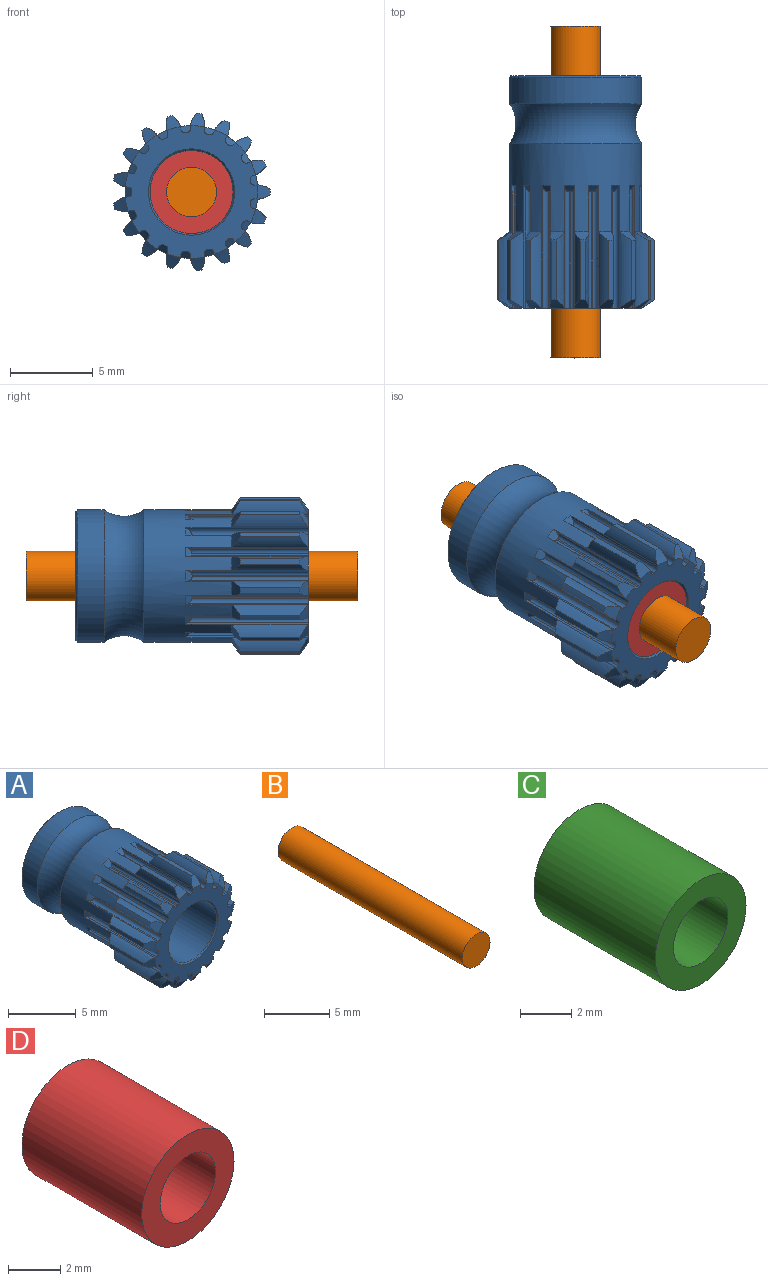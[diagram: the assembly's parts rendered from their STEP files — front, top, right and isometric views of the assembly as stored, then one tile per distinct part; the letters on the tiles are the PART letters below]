
ASSEMBLY  parts=4 mates=3
PART A: 196 faces, bbox 9.5x14x9.5 mm
  f0: cone r=4.38mm half-angle=56.3deg, axis (0,-1,0), area 0.6mm2, adj f21,f42,f43,f88
  f1: cone r=4.38mm half-angle=56.3deg, axis (0,-1,0), area 0.6mm2, adj f24,f50,f51,f88
  f2: cone r=4.38mm half-angle=56.3deg, axis (0,-1,0), area 0.6mm2, adj f25,f53,f54,f88
  f3: cone r=4.38mm half-angle=56.3deg, axis (0,-1,0), area 0.6mm2, adj f26,f59,f60,f88
  f4: cone r=4.38mm half-angle=56.3deg, axis (0,-1,0), area 0.6mm2, adj f12,f62,f63,f88
  f5: cone r=4.38mm half-angle=56.3deg, axis (0,-1,0), area 0.6mm2, adj f13,f65,f66,f88
  f6: cone r=4.38mm half-angle=56.3deg, axis (0,-1,0), area 0.6mm2, adj f14,f68,f69,f88
  f7: cone r=4.38mm half-angle=56.3deg, axis (0,-1,0), area 0.6mm2, adj f15,f82,f83,f88
  f8: cone r=4.38mm half-angle=56.3deg, axis (0,-1,0), area 0.6mm2, adj f16,f17,f80,f88
  f9: cone r=4.38mm half-angle=56.3deg, axis (0,-1,0), area 0.6mm2, adj f18,f77,f78,f88
  f10: cone r=4.38mm half-angle=56.3deg, axis (0,-1,0), area 0.6mm2, adj f19,f74,f75,f88
  f11: cone r=4.38mm half-angle=56.3deg, axis (0,-1,0), area 0.6mm2, adj f20,f39,f40,f88
  f12: extruded ~7x0.63mm, area 3.4mm2, adj f4,f30,f61,f63,f88,f111
  f13: extruded ~7x0.78mm, area 3.4mm2, adj f5,f30,f64,f66,f88,f116
  f14: extruded ~7x0.82mm, area 3.4mm2, adj f6,f30,f67,f69,f88,f121
  f15: extruded ~7x0.75mm, area 3.4mm2, adj f7,f30,f81,f83,f88,f126
  f16: extruded ~7x0.81mm, area 3.4mm2, adj f8,f30,f79,f80,f88,f130
  f17: extruded ~7x0.58mm, area 3.4mm2, adj f8,f30,f79,f80,f88,f131
  f18: extruded ~7x0.75mm, area 3.4mm2, adj f9,f30,f76,f78,f88,f136
  f19: extruded ~7x0.82mm, area 3.4mm2, adj f10,f30,f73,f75,f88,f141
  f20: extruded ~7x0.72mm, area 3.4mm2, adj f11,f30,f38,f40,f88,f157
  f21: extruded ~7x0.81mm, area 3.4mm2, adj f0,f30,f41,f43,f88,f162
  f22: extruded ~7x0.63mm, area 3.4mm2, adj f23,f30,f44,f45,f88,f166
  f23: cone r=4.38mm half-angle=56.3deg, axis (0,-1,0), area 0.6mm2, adj f22,f45,f88,f167
  f24: extruded ~7x0.68mm, area 3.4mm2, adj f1,f30,f49,f51,f88,f179
  f25: extruded ~7x0.8mm, area 3.4mm2, adj f2,f30,f52,f54,f88,f184
  f26: extruded ~7x0.71mm, area 3.4mm2, adj f3,f30,f58,f60,f88,f194
  f27: extruded ~7x0.78mm, area 3.4mm2, adj f30,f70,f72,f88,f146,f195
  f28: cone r=2.55mm half-angle=45deg, axis (0,-1,0), area 2.3mm2, adj f29,f30
  f29: cylinder r=2.5mm len=13.8mm, axis (0,1,0), area 216.8mm2, adj f28,f31
  f30: plane 8x7.99mm, normal (0,-1,0), area 25.4mm2, adj f12,f13,f14,f15,f16,f17,f18,f19
  f31: cone r=2.55mm half-angle=45deg, axis (0,1,0), area 2.3mm2, adj f29,f32
  f32: plane 7.8x7.8mm, normal (0,1,0), area 26.5mm2, adj f31,f33
  f33: cone r=3.95mm half-angle=45deg, axis (0,-1,0), area 3.5mm2, adj f32,f34
  f34: cylinder r=4mm len=8mm, axis (0,1,0), area 40.2mm2, adj f33,f87
  f35: cone r=4.38mm half-angle=56.3deg, axis (0,1,0), area 0.6mm2, adj f30,f36,f37,f151
  f36: extruded ~7x0.8mm, area 3.4mm2, adj f30,f35,f37,f86,f88,f150
  f37: cylinder r=4.75mm len=3.6mm, axis (0,1,0), area 1.2mm2, adj f35,f36,f86,f151
  f38: cone r=4.38mm half-angle=56.3deg, axis (0,1,0), area 0.6mm2, adj f20,f30,f39,f40
  f39: extruded ~7x0.81mm, area 3.4mm2, adj f11,f30,f38,f40,f88,f156
  f40: cylinder r=4.75mm len=3.6mm, axis (0,1,0), area 1.2mm2, adj f11,f20,f38,f39
  f41: cone r=4.38mm half-angle=56.3deg, axis (0,1,0), area 0.6mm2, adj f21,f30,f42,f43
  f42: extruded ~7x0.72mm, area 3.4mm2, adj f0,f30,f41,f43,f88,f161
  f43: cylinder r=4.75mm len=3.6mm, axis (0,1,0), area 1.2mm2, adj f0,f21,f41,f42
  f44: cone r=4.38mm half-angle=56.3deg, axis (0,1,0), area 0.6mm2, adj f22,f30,f45,f167
  f45: cylinder r=4.75mm len=3.6mm, axis (0,1,0), area 1.2mm2, adj f22,f23,f44,f167
  f46: cone r=4.38mm half-angle=56.3deg, axis (0,1,0), area 0.6mm2, adj f30,f47,f48,f173
  f47: extruded ~7x0.78mm, area 3.4mm2, adj f30,f46,f48,f84,f88,f172
  f48: cylinder r=4.75mm len=3.6mm, axis (0,1,0), area 1.2mm2, adj f46,f47,f84,f173
  f49: cone r=4.38mm half-angle=56.3deg, axis (0,1,0), area 0.6mm2, adj f24,f30,f50,f51
  f50: extruded ~7x0.82mm, area 3.4mm2, adj f1,f30,f49,f51,f88,f178
  f51: cylinder r=4.75mm len=3.6mm, axis (0,1,0), area 1.2mm2, adj f1,f24,f49,f50
  f52: cone r=4.38mm half-angle=56.3deg, axis (0,1,0), area 0.6mm2, adj f25,f30,f53,f54
  f53: extruded ~7x0.75mm, area 3.4mm2, adj f2,f30,f52,f54,f88,f183
  f54: cylinder r=4.75mm len=3.6mm, axis (0,1,0), area 1.2mm2, adj f2,f25,f52,f53
  f55: cone r=4.38mm half-angle=56.3deg, axis (0,1,0), area 0.6mm2, adj f30,f56,f57,f106
  f56: extruded ~7x0.58mm, area 3.4mm2, adj f30,f55,f57,f85,f88,f188
  f57: cylinder r=4.75mm len=3.6mm, axis (0,1,0), area 1.2mm2, adj f55,f56,f85,f106
  f58: cone r=4.38mm half-angle=56.3deg, axis (0,1,0), area 0.6mm2, adj f26,f30,f59,f60
  f59: extruded ~7x0.75mm, area 3.4mm2, adj f3,f30,f58,f60,f88,f193
  f60: cylinder r=4.75mm len=3.6mm, axis (0,1,0), area 1.2mm2, adj f3,f26,f58,f59
  f61: cone r=4.38mm half-angle=56.3deg, axis (0,1,0), area 0.6mm2, adj f12,f30,f62,f63
  f62: extruded ~7x0.82mm, area 3.4mm2, adj f4,f30,f61,f63,f88,f110
  f63: cylinder r=4.75mm len=3.6mm, axis (0,1,0), area 1.2mm2, adj f4,f12,f61,f62
  f64: cone r=4.38mm half-angle=56.3deg, axis (0,1,0), area 0.6mm2, adj f13,f30,f65,f66
  f65: extruded ~7x0.78mm, area 3.4mm2, adj f5,f30,f64,f66,f88,f115
  f66: cylinder r=4.75mm len=3.6mm, axis (0,1,0), area 1.2mm2, adj f5,f13,f64,f65
  f67: cone r=4.38mm half-angle=56.3deg, axis (0,1,0), area 0.6mm2, adj f14,f30,f68,f69
  f68: extruded ~7x0.63mm, area 3.4mm2, adj f6,f30,f67,f69,f88,f120
  f69: cylinder r=4.75mm len=3.6mm, axis (0,1,0), area 1.2mm2, adj f6,f14,f67,f68
  f70: cone r=4.38mm half-angle=56.3deg, axis (0,1,0), area 0.6mm2, adj f27,f30,f71,f72
  f71: extruded ~7x0.67mm, area 3.4mm2, adj f30,f70,f72,f88,f145,f195
  f72: cylinder r=4.75mm len=3.6mm, axis (0,1,0), area 1.2mm2, adj f27,f70,f71,f195
  f73: cone r=4.38mm half-angle=56.3deg, axis (0,1,0), area 0.6mm2, adj f19,f30,f74,f75
  f74: extruded ~7x0.68mm, area 3.4mm2, adj f10,f30,f73,f75,f88,f140
  f75: cylinder r=4.75mm len=3.6mm, axis (0,1,0), area 1.2mm2, adj f10,f19,f73,f74
  f76: cone r=4.38mm half-angle=56.3deg, axis (0,1,0), area 0.6mm2, adj f18,f30,f77,f78
  f77: extruded ~7x0.8mm, area 3.4mm2, adj f9,f30,f76,f78,f88,f135
  f78: cylinder r=4.75mm len=3.6mm, axis (0,1,0), area 1.2mm2, adj f9,f18,f76,f77
  f79: cone r=4.38mm half-angle=56.3deg, axis (0,1,0), area 0.6mm2, adj f16,f17,f30,f80
  f80: cylinder r=4.75mm len=3.6mm, axis (0,1,0), area 1.2mm2, adj f8,f16,f17,f79
  f81: cone r=4.38mm half-angle=56.3deg, axis (0,1,0), area 0.6mm2, adj f15,f30,f82,f83
  f82: extruded ~7x0.71mm, area 3.4mm2, adj f7,f30,f81,f83,f88,f125
  f83: cylinder r=4.75mm len=3.6mm, axis (0,1,0), area 1.2mm2, adj f7,f15,f81,f82
  f84: cone r=4.38mm half-angle=56.3deg, axis (0,-1,0), area 0.6mm2, adj f47,f48,f88,f173
  f85: cone r=4.38mm half-angle=56.3deg, axis (0,-1,0), area 0.6mm2, adj f56,f57,f88,f106
  f86: cone r=4.38mm half-angle=56.3deg, axis (0,-1,0), area 0.6mm2, adj f36,f37,f88,f151
  f87: torus R=5.6mm, axis (0,-1,0), area 60.4mm2, adj f34,f88
  f88: cylinder r=4mm len=8mm, axis (0,1,0), area 103.7mm2, adj f0,f1,f2,f3,f4,f5,f6,f7
  f89: cone r=3.8mm half-angle=45deg, axis (0,1,0), area 0.3mm2, adj f88,f131,f132,f133,f134,f135
  f90: cone r=3.8mm half-angle=45deg, axis (0,1,0), area 0.3mm2, adj f88,f126,f127,f128,f129,f130
  f91: cone r=3.8mm half-angle=45deg, axis (0,1,0), area 0.3mm2, adj f88,f121,f122,f123,f124,f125
  f92: cone r=3.8mm half-angle=45deg, axis (0,1,0), area 0.3mm2, adj f88,f116,f117,f118,f119,f120
  f93: cone r=3.8mm half-angle=45deg, axis (0,1,0), area 0.3mm2, adj f88,f111,f112,f113,f114,f115
  f94: cone r=3.8mm half-angle=45deg, axis (0,1,0), area 0.3mm2, adj f88,f107,f108,f109,f110,f194
  f95: cone r=3.8mm half-angle=45deg, axis (0,1,0), area 0.3mm2, adj f88,f189,f190,f191,f192,f193
  f96: cone r=3.8mm half-angle=45deg, axis (0,1,0), area 0.3mm2, adj f88,f184,f185,f186,f187,f188
  f97: cone r=3.8mm half-angle=45deg, axis (0,1,0), area 0.3mm2, adj f88,f179,f180,f181,f182,f183
  f98: cone r=3.8mm half-angle=45deg, axis (0,1,0), area 0.3mm2, adj f88,f174,f175,f176,f177,f178
  f99: cone r=3.8mm half-angle=45deg, axis (0,1,0), area 0.3mm2, adj f88,f168,f169,f170,f171,f172
  f100: cone r=3.8mm half-angle=45deg, axis (0,1,0), area 0.3mm2, adj f88,f136,f137,f138,f139,f140
  f101: cone r=3.8mm half-angle=45deg, axis (0,1,0), area 0.3mm2, adj f88,f141,f142,f143,f144,f145
  f102: cone r=3.8mm half-angle=45deg, axis (0,1,0), area 0.3mm2, adj f88,f146,f147,f148,f149,f150
  f103: cone r=3.8mm half-angle=45deg, axis (0,1,0), area 0.3mm2, adj f88,f152,f153,f154,f155,f156
  f104: cone r=3.8mm half-angle=45deg, axis (0,1,0), area 0.3mm2, adj f88,f157,f158,f159,f160,f161
  f105: cone r=3.8mm half-angle=45deg, axis (0,1,0), area 0.3mm2, adj f88,f162,f163,f164,f165,f166
  f106: extruded ~7x0.81mm, area 3.4mm2, adj f30,f55,f57,f85,f88,f189
  f107: cylinder r=0.25mm len=7.24mm, axis (0,1,0), area 2.7mm2, adj f30,f94,f108,f194
  f108: cylinder r=3.6mm len=7mm, axis (0,1,0), area 0.6mm2, adj f30,f94,f107,f109
  f109: cylinder r=0.25mm len=7.24mm, axis (0,1,0), area 2.7mm2, adj f30,f94,f108,f110
  f110: plane 7.4x0.14mm, normal (-0.46,0,0.89), area 1.1mm2, adj f30,f62,f88,f94,f109
  f111: plane 7.4x0.15mm, normal (0.26,0,-0.97), area 1.1mm2, adj f12,f30,f88,f93,f112
  f112: cylinder r=0.25mm len=7.24mm, axis (0,1,0), area 2.7mm2, adj f30,f93,f111,f113
  f113: cylinder r=3.6mm len=7mm, axis (0,1,0), area 0.6mm2, adj f30,f93,f112,f114
  f114: cylinder r=0.25mm len=7.24mm, axis (0,1,0), area 2.7mm2, adj f30,f93,f113,f115
  f115: plane 7.4x0.16mm, normal (-0.1,0,0.99), area 1.1mm2, adj f30,f65,f88,f93,f114
  f116: plane 7.4x0.16mm, normal (-0.1,0,-0.99), area 1.1mm2, adj f13,f30,f88,f92,f117
  f117: cylinder r=0.25mm len=7.24mm, axis (0,1,0), area 2.7mm2, adj f30,f92,f116,f118
  f118: cylinder r=3.6mm len=7mm, axis (0,1,0), area 0.6mm2, adj f30,f92,f117,f119
  f119: cylinder r=0.25mm len=7.24mm, axis (0,1,0), area 2.7mm2, adj f30,f92,f118,f120
  f120: plane 7.4x0.15mm, normal (0.26,0,0.97), area 1.1mm2, adj f30,f68,f88,f92,f119
  f121: plane 7.4x0.14mm, normal (-0.46,0,-0.89), area 1.1mm2, adj f14,f30,f88,f91,f122
  f122: cylinder r=0.25mm len=7.24mm, axis (0,1,0), area 2.7mm2, adj f30,f91,f121,f123
  f123: cylinder r=3.6mm len=7mm, axis (0,1,0), area 0.6mm2, adj f30,f91,f122,f124
  f124: cylinder r=0.25mm len=7.24mm, axis (0,1,0), area 2.7mm2, adj f30,f91,f123,f125
  f125: plane 7.4x0.13mm, normal (0.59,0,0.81), area 1.1mm2, adj f30,f82,f88,f91,f124
  f126: plane 7.4x0.12mm, normal (-0.75,0,-0.66), area 1.1mm2, adj f15,f30,f88,f90,f127
  f127: cylinder r=0.25mm len=7.24mm, axis (0,1,0), area 2.7mm2, adj f30,f90,f126,f128
  f128: cylinder r=3.6mm len=7mm, axis (0,1,0), area 0.6mm2, adj f30,f90,f127,f129
  f129: cylinder r=0.25mm len=7.24mm, axis (0,1,0), area 2.7mm2, adj f30,f90,f128,f130
  f130: plane 7.4x0.13mm, normal (0.84,0,0.54), area 1.1mm2, adj f16,f30,f88,f90,f129
  f131: plane 7.4x0.15mm, normal (-0.94,0,-0.35), area 1.1mm2, adj f17,f30,f88,f89,f132
  f132: cylinder r=0.25mm len=7.24mm, axis (0,1,0), area 2.7mm2, adj f30,f89,f131,f133
  f133: cylinder r=3.6mm len=7mm, axis (0,1,0), area 0.6mm2, adj f30,f89,f132,f134
  f134: cylinder r=0.25mm len=7.24mm, axis (0,1,0), area 2.7mm2, adj f30,f89,f133,f135
  f135: plane 7.4x0.16mm, normal (0.98,0,0.2), area 1.1mm2, adj f30,f77,f88,f89,f134
  f136: plane 7.4x0.16mm, normal (-1,0,0.01), area 1.1mm2, adj f18,f30,f88,f100,f137
  f137: cylinder r=0.25mm len=7.24mm, axis (0,1,0), area 2.7mm2, adj f30,f100,f136,f138
  f138: cylinder r=3.6mm len=7mm, axis (0,1,0), area 0.6mm2, adj f30,f100,f137,f139
  f139: cylinder r=0.25mm len=7.24mm, axis (0,1,0), area 2.7mm2, adj f30,f100,f138,f140
  f140: plane 7.4x0.16mm, normal (0.99,0,-0.17), area 1.1mm2, adj f30,f74,f88,f100,f139
  f141: plane 7.4x0.15mm, normal (-0.93,0,0.37), area 1.1mm2, adj f19,f30,f88,f101,f142
  f142: cylinder r=0.25mm len=7.24mm, axis (0,1,0), area 2.7mm2, adj f30,f101,f141,f143
  f143: cylinder r=3.6mm len=7mm, axis (0,1,0), area 0.6mm2, adj f30,f101,f142,f144
  f144: cylinder r=0.25mm len=7.24mm, axis (0,1,0), area 2.7mm2, adj f30,f101,f143,f145
  f145: plane 7.4x0.14mm, normal (0.86,0,-0.52), area 1.1mm2, adj f30,f71,f88,f101,f144
  f146: plane 7.4x0.12mm, normal (-0.73,0,0.68), area 1.1mm2, adj f27,f30,f88,f102,f147
  f147: cylinder r=0.25mm len=7.24mm, axis (0,1,0), area 2.7mm2, adj f30,f102,f146,f148
  f148: cylinder r=3.6mm len=7mm, axis (0,1,0), area 0.6mm2, adj f30,f102,f147,f149
  f149: cylinder r=0.25mm len=7.24mm, axis (0,1,0), area 2.7mm2, adj f30,f102,f148,f150
  f150: plane 7.4x0.13mm, normal (0.61,0,-0.79), area 1.1mm2, adj f30,f36,f88,f102,f149
  f151: extruded ~7x0.63mm, area 3.4mm2, adj f30,f35,f37,f86,f88,f152
  f152: plane 7.4x0.14mm, normal (-0.43,0,0.9), area 1.1mm2, adj f30,f88,f103,f151,f153
  f153: cylinder r=0.25mm len=7.24mm, axis (0,1,0), area 2.7mm2, adj f30,f103,f152,f154
  f154: cylinder r=3.6mm len=7mm, axis (0,1,0), area 0.6mm2, adj f30,f103,f153,f155
  f155: cylinder r=0.25mm len=7.24mm, axis (0,1,0), area 2.7mm2, adj f30,f103,f154,f156
  f156: plane 7.4x0.15mm, normal (0.29,0,-0.96), area 1.1mm2, adj f30,f39,f88,f103,f155
  f157: plane 7.4x0.16mm, normal (-0.08,0,1), area 1.1mm2, adj f20,f30,f88,f104,f158
  f158: cylinder r=0.25mm len=7.24mm, axis (0,1,0), area 2.7mm2, adj f30,f104,f157,f159
  f159: cylinder r=3.6mm len=7mm, axis (0,1,0), area 0.6mm2, adj f30,f104,f158,f160
  f160: cylinder r=0.25mm len=7.24mm, axis (0,1,0), area 2.7mm2, adj f30,f104,f159,f161
  f161: plane 7.4x0.16mm, normal (-0.08,0,-1), area 1.1mm2, adj f30,f42,f88,f104,f160
  f162: plane 7.4x0.15mm, normal (0.29,0,0.96), area 1.1mm2, adj f21,f30,f88,f105,f163
  f163: cylinder r=0.25mm len=7.24mm, axis (0,1,0), area 2.7mm2, adj f30,f105,f162,f164
  f164: cylinder r=3.6mm len=7mm, axis (0,1,0), area 0.6mm2, adj f30,f105,f163,f165
  f165: cylinder r=0.25mm len=7.24mm, axis (0,1,0), area 2.7mm2, adj f30,f105,f164,f166
  f166: plane 7.4x0.14mm, normal (-0.43,0,-0.9), area 1.1mm2, adj f22,f30,f88,f105,f165
  f167: extruded ~7x0.8mm, area 3.4mm2, adj f23,f30,f44,f45,f88,f168
  f168: plane 7.4x0.13mm, normal (0.61,0,0.79), area 1.1mm2, adj f30,f88,f99,f167,f169
  f169: cylinder r=0.25mm len=7.24mm, axis (0,1,0), area 2.7mm2, adj f30,f99,f168,f170
  f170: cylinder r=3.6mm len=7mm, axis (0,1,0), area 0.6mm2, adj f30,f99,f169,f171
  f171: cylinder r=0.25mm len=7.24mm, axis (0,1,0), area 2.7mm2, adj f30,f99,f170,f172
  f172: plane 7.4x0.12mm, normal (-0.73,0,-0.68), area 1.1mm2, adj f30,f47,f88,f99,f171
  f173: extruded ~7x0.67mm, area 3.4mm2, adj f30,f46,f48,f84,f88,f174
  f174: plane 7.4x0.14mm, normal (0.86,0,0.52), area 1.1mm2, adj f30,f88,f98,f173,f175
  f175: cylinder r=0.25mm len=7.24mm, axis (0,1,0), area 2.7mm2, adj f30,f98,f174,f176
  f176: cylinder r=3.6mm len=7mm, axis (0,1,0), area 0.6mm2, adj f30,f98,f175,f177
  f177: cylinder r=0.25mm len=7.24mm, axis (0,1,0), area 2.7mm2, adj f30,f98,f176,f178
  f178: plane 7.4x0.15mm, normal (-0.93,0,-0.37), area 1.1mm2, adj f30,f50,f88,f98,f177
  f179: plane 7.4x0.16mm, normal (0.99,0,0.17), area 1.1mm2, adj f24,f30,f88,f97,f180
  f180: cylinder r=0.25mm len=7.24mm, axis (0,1,0), area 2.7mm2, adj f30,f97,f179,f181
  f181: cylinder r=3.6mm len=7mm, axis (0,1,0), area 0.6mm2, adj f30,f97,f180,f182
  f182: cylinder r=0.25mm len=7.24mm, axis (0,1,0), area 2.7mm2, adj f30,f97,f181,f183
  f183: plane 7.4x0.16mm, normal (-1,0,-0.01), area 1.1mm2, adj f30,f53,f88,f97,f182
  f184: plane 7.4x0.16mm, normal (0.98,0,-0.2), area 1.1mm2, adj f25,f30,f88,f96,f185
  f185: cylinder r=0.25mm len=7.24mm, axis (0,1,0), area 2.7mm2, adj f30,f96,f184,f186
  f186: cylinder r=3.6mm len=7mm, axis (0,1,0), area 0.6mm2, adj f30,f96,f185,f187
  f187: cylinder r=0.25mm len=7.24mm, axis (0,1,0), area 2.7mm2, adj f30,f96,f186,f188
  f188: plane 7.4x0.15mm, normal (-0.94,0,0.35), area 1.1mm2, adj f30,f56,f88,f96,f187
  f189: plane 7.4x0.13mm, normal (0.84,0,-0.54), area 1.1mm2, adj f30,f88,f95,f106,f190
  f190: cylinder r=0.25mm len=7.24mm, axis (0,1,0), area 2.7mm2, adj f30,f95,f189,f191
  f191: cylinder r=3.6mm len=7mm, axis (0,1,0), area 0.6mm2, adj f30,f95,f190,f192
  f192: cylinder r=0.25mm len=7.24mm, axis (0,1,0), area 2.7mm2, adj f30,f95,f191,f193
  f193: plane 7.4x0.12mm, normal (-0.75,0,0.66), area 1.1mm2, adj f30,f59,f88,f95,f192
  f194: plane 7.4x0.13mm, normal (0.59,0,-0.81), area 1.1mm2, adj f26,f30,f88,f94,f107
  f195: cone r=4.38mm half-angle=56.3deg, axis (0,-1,0), area 0.6mm2, adj f27,f71,f72,f88
PART B: 3 faces, bbox 3x20x3 mm
  f0: cylinder r=1.5mm len=20mm, axis (0,1,0), area 188.5mm2, adj f1,f2
  f1: plane 3x3mm, normal (0,1,0), area 7.1mm2, adj f0
  f2: plane 3x3mm, normal (0,-1,0), area 7.1mm2, adj f0
PART C: 4 faces, bbox 5x6.7x5 mm
  f0: cylinder r=1.5mm len=6.7mm, axis (0,1,0), area 63.1mm2, adj f2,f3
  f1: cylinder r=2.5mm len=6.7mm, axis (0,1,0), area 105.2mm2, adj f2,f3
  f2: plane 5x5mm, normal (0,1,0), area 12.6mm2, adj f0,f1
  f3: plane 5x5mm, normal (0,-1,0), area 12.6mm2, adj f0,f1
PART D: 4 faces, bbox 5x6.5x5 mm
  f0: cylinder r=1.5mm len=6.5mm, axis (0,1,0), area 61.3mm2, adj f2,f3
  f1: cylinder r=2.5mm len=6.5mm, axis (0,1,0), area 102.1mm2, adj f2,f3
  f2: plane 5x5mm, normal (0,1,0), area 12.6mm2, adj f0,f1
  f3: plane 5x5mm, normal (0,-1,0), area 12.6mm2, adj f0,f1
PLACE A t=(0.9,-5.55,0.66)mm
PLACE B t=(0.9,-5.55,0.66)mm
PLACE C t=(0.9,-5.45,0.66)mm
PLACE D t=(0.9,-5.65,0.66)mm
MATE revolute B.f0 <-> A.f0  axis (0,1,0) through (9.4,1.45,0.66)mm
MATE fastened C.f0 <-> A.f0  axis (0,1,0) through (9.4,8.35,0.66)mm
MATE fastened D.f0 <-> A.f0  axis (0,-1,0) through (9.4,-5.45,0.66)mm
